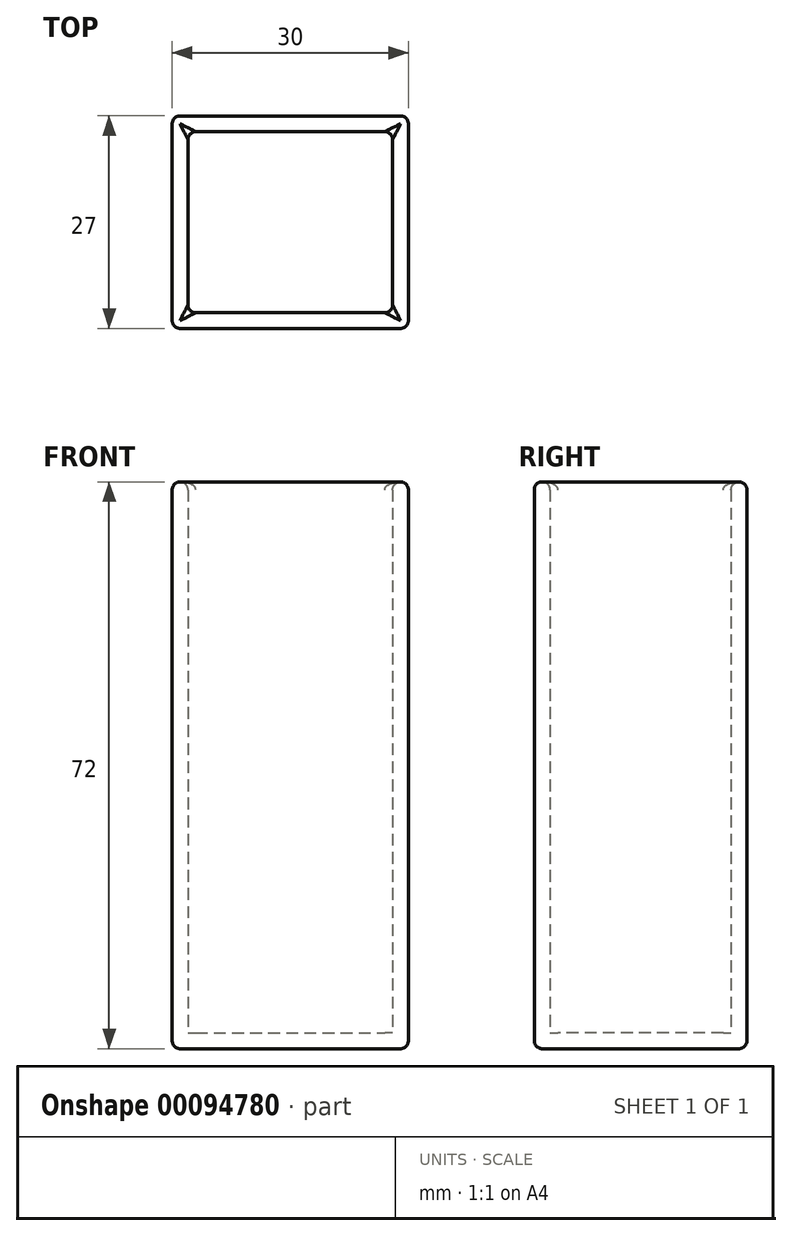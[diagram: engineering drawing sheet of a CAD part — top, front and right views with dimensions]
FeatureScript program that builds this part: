
annotation { "Feature Type Name" : "Feature", "Feature Type Description" : "" }
export const myFeature = defineFeature(function(context is Context, id is Id, definition is map)
    precondition{}
    {
        {
            var Q0;
            Q0=qCreatedBy(makeId("Top.planeOp"),FACE);
            var sketch = newSketch(context, id + "F0", { "sketchPlane" : qUnion([Q0])});
            skLineSegment(sketch, "E0.bottom", {"start": v(-23.26, 7.45) * mm, "end": v(2.74, 7.45) * mm});
            skLineSegment(sketch, "E0.top", {"start": v(-23.26, -15.55) * mm, "end": v(2.74, -15.55) * mm});
            skLineSegment(sketch, "E0.left", {"start": v(-23.26, 7.45) * mm, "end": v(-23.26, -15.55) * mm});
            skLineSegment(sketch, "E0.right", {"start": v(2.74, 7.45) * mm, "end": v(2.74, -15.55) * mm});
            skLineSegment(sketch, "E1.0", {"start": v(-25.26, 9.45) * mm, "end": v(4.74, 9.45) * mm});
            skLineSegment(sketch, "E1.1", {"start": v(-25.26, 9.45) * mm, "end": v(-25.26, -17.55) * mm});
            skLineSegment(sketch, "E1.2", {"start": v(-25.26, -17.55) * mm, "end": v(4.74, -17.55) * mm});
            skLineSegment(sketch, "E1.3", {"start": v(4.74, 9.45) * mm, "end": v(4.74, -17.55) * mm});
            skSolve(sketch);
        }
        {
            var Q0;
            Q0=makeQuery(id+"F0.imprint","IMPRINT",FACE,{"disambiguationData":[TD([[makeQuery(id+"F0.imprint","IMPRINT",EDGE,{"derivedFrom":sQuery(id+"F0.wireOp",EDGE,"E0.bottom")}),1.0]])]});
            extrude(context, id + "F1", {"entities" : qUnion([Q0]), "depth" : 70 * mm});
        }
        {
            var Q0;
            Q0=makeQuery(id+"F1.opExtrude","CAP_FACE",FACE,{"disambiguationData":[OSD([sQuery(id+"F0.wireOp",EDGE,"E0.bottom"),sQuery(id+"F0.wireOp",EDGE,"E0.top"),sQuery(id+"F0.wireOp",EDGE,"E0.left"),sQuery(id+"F0.wireOp",EDGE,"E0.right"),sQuery(id+"F0.wireOp",EDGE,"E1.0"),sQuery(id+"F0.wireOp",EDGE,"E1.1"),sQuery(id+"F0.wireOp",EDGE,"E1.2"),sQuery(id+"F0.wireOp",EDGE,"E1.3")])],"isStart":true});
            var sketch = newSketch(context, id + "F2", { "sketchPlane" : qUnion([Q0])});
            skLineSegment(sketch, "E2.bottom", {"start": v(-25.26, -9.45) * mm, "end": v(4.74, -9.45) * mm});
            skLineSegment(sketch, "E2.top", {"start": v(-25.26, 17.55) * mm, "end": v(4.74, 17.55) * mm});
            skLineSegment(sketch, "E2.left", {"start": v(-25.26, -9.45) * mm, "end": v(-25.26, 17.55) * mm});
            skLineSegment(sketch, "E2.right", {"start": v(4.74, -9.45) * mm, "end": v(4.74, 17.55) * mm});
            skSolve(sketch);
        }
        {
            var Q0;
            Q0 = qSketchRegion(id + "F2", true);
            extrude(context, id + "F3", {"entities" : qUnion([Q0]), "operationType" : NewBodyOperationType.ADD, "depth" : 2 * mm});
        }
        {
            var Q0;
            Q0=makeQuery(id+"F3.opExtrude","CAP_FACE",FACE,{"disambiguationData":[OSD([sQuery(id+"F2.wireOp",EDGE,"E2.bottom"),sQuery(id+"F2.wireOp",EDGE,"E2.top"),sQuery(id+"F2.wireOp",EDGE,"E2.left"),sQuery(id+"F2.wireOp",EDGE,"E2.right")])],"isStart":false});
            var Q1;
            Q1=makeQuery(id+"F3.boolean.opBoolean","MERGE",EDGE,{"derivedFrom":[makeQuery(id+"F1.opExtrude","SWEPT_EDGE",EDGE,{"disambiguationData":[OSD([sQuery(id+"F0.wireOp",EDGE,"E1.1"),sQuery(id+"F0.wireOp",EDGE,"E1.2")])]}),makeQuery(id+"F3.opExtrude","SWEPT_EDGE",EDGE,{"disambiguationData":[OSD([sQuery(id+"F2.wireOp",EDGE,"E2.top"),sQuery(id+"F2.wireOp",EDGE,"E2.left")])]})]});
            var Q2;
            Q2=makeQuery(id+"F3.boolean.opBoolean","MERGE",EDGE,{"derivedFrom":[makeQuery(id+"F1.opExtrude","SWEPT_EDGE",EDGE,{"disambiguationData":[OSD([sQuery(id+"F0.wireOp",EDGE,"E1.0"),sQuery(id+"F0.wireOp",EDGE,"E1.1")])]}),makeQuery(id+"F3.opExtrude","SWEPT_EDGE",EDGE,{"disambiguationData":[OSD([sQuery(id+"F2.wireOp",EDGE,"E2.bottom"),sQuery(id+"F2.wireOp",EDGE,"E2.left")])]})]});
            var Q3;
            Q3=makeQuery(id+"F3.boolean.opBoolean","MERGE",EDGE,{"derivedFrom":[makeQuery(id+"F1.opExtrude","SWEPT_EDGE",EDGE,{"disambiguationData":[OSD([sQuery(id+"F0.wireOp",EDGE,"E1.2"),sQuery(id+"F0.wireOp",EDGE,"E1.3")])]}),makeQuery(id+"F3.opExtrude","SWEPT_EDGE",EDGE,{"disambiguationData":[OSD([sQuery(id+"F2.wireOp",EDGE,"E2.top"),sQuery(id+"F2.wireOp",EDGE,"E2.right")])]})]});
            var Q4;
            Q4=makeQuery(id+"F3.boolean.opBoolean","MERGE",EDGE,{"derivedFrom":[makeQuery(id+"F1.opExtrude","SWEPT_EDGE",EDGE,{"disambiguationData":[OSD([sQuery(id+"F0.wireOp",EDGE,"E1.0"),sQuery(id+"F0.wireOp",EDGE,"E1.3")])]}),makeQuery(id+"F3.opExtrude","SWEPT_EDGE",EDGE,{"disambiguationData":[OSD([sQuery(id+"F2.wireOp",EDGE,"E2.bottom"),sQuery(id+"F2.wireOp",EDGE,"E2.right")])]})]});
            var Q5;
            Q5=makeQuery(id+"F1.opExtrude","CAP_EDGE",EDGE,{"disambiguationData":[OSD([sQuery(id+"F0.wireOp",EDGE,"E1.2")])],"isStart":false});
            var Q6;
            Q6=makeQuery(id+"F1.opExtrude","CAP_EDGE",EDGE,{"disambiguationData":[OSD([sQuery(id+"F0.wireOp",EDGE,"E1.3")])],"isStart":false});
            var Q7;
            Q7=makeQuery(id+"F1.opExtrude","CAP_EDGE",EDGE,{"disambiguationData":[OSD([sQuery(id+"F0.wireOp",EDGE,"E1.0")])],"isStart":false});
            var Q8;
            Q8=makeQuery(id+"F1.opExtrude","CAP_EDGE",EDGE,{"disambiguationData":[OSD([sQuery(id+"F0.wireOp",EDGE,"E1.1")])],"isStart":false});
            var Q9;
            Q9=makeQuery(id+"F1.opExtrude","CAP_EDGE",EDGE,{"disambiguationData":[OSD([sQuery(id+"F0.wireOp",EDGE,"E0.top")])],"isStart":false});
            var Q10;
            Q10=makeQuery(id+"F1.opExtrude","CAP_EDGE",EDGE,{"disambiguationData":[OSD([sQuery(id+"F0.wireOp",EDGE,"E0.right")])],"isStart":false});
            var Q11;
            Q11=makeQuery(id+"F1.opExtrude","CAP_EDGE",EDGE,{"disambiguationData":[OSD([sQuery(id+"F0.wireOp",EDGE,"E0.bottom")])],"isStart":false});
            var Q12;
            Q12=makeQuery(id+"F1.opExtrude","CAP_EDGE",EDGE,{"disambiguationData":[OSD([sQuery(id+"F0.wireOp",EDGE,"E0.left")])],"isStart":false});
            fillet(context, id + "F4", {"entities" : qUnion([Q0, Q1, Q2, Q3, Q4, Q5, Q6, Q7, Q8, Q9, Q10, Q11, Q12]), "radius" : 1 * mm, "tangentPropagation" : true, "allowEdgeOverflow" : false});
        }
        {
            var Q0;
            Q0=makeQuery(id+"F1.opExtrude","SWEPT_EDGE",EDGE,{"disambiguationData":[OSD([sQuery(id+"F0.wireOp",EDGE,"E0.top"),sQuery(id+"F0.wireOp",EDGE,"E0.left")])]});
            var Q1;
            Q1=makeQuery(id+"F1.opExtrude","CAP_EDGE",EDGE,{"disambiguationData":[OSD([sQuery(id+"F0.wireOp",EDGE,"E0.top")])],"isStart":true});
            var Q2;
            Q2=makeQuery(id+"F1.opExtrude","SWEPT_EDGE",EDGE,{"disambiguationData":[OSD([sQuery(id+"F0.wireOp",EDGE,"E0.top"),sQuery(id+"F0.wireOp",EDGE,"E0.right")])]});
            var Q3;
            Q3=makeQuery(id+"F1.opExtrude","SWEPT_EDGE",EDGE,{"disambiguationData":[OSD([sQuery(id+"F0.wireOp",EDGE,"E0.bottom"),sQuery(id+"F0.wireOp",EDGE,"E0.right")])]});
            var Q4;
            Q4=makeQuery(id+"F1.opExtrude","SWEPT_EDGE",EDGE,{"disambiguationData":[OSD([sQuery(id+"F0.wireOp",EDGE,"E0.bottom"),sQuery(id+"F0.wireOp",EDGE,"E0.left")])]});
            var Q5;
            Q5=makeQuery(id+"F1.opExtrude","CAP_EDGE",EDGE,{"disambiguationData":[OSD([sQuery(id+"F0.wireOp",EDGE,"E0.left")])],"isStart":true});
            var Q6;
            Q6=makeQuery(id+"F1.opExtrude","CAP_EDGE",EDGE,{"disambiguationData":[OSD([sQuery(id+"F0.wireOp",EDGE,"E0.bottom")])],"isStart":true});
            fillet(context, id + "F5", {"entities" : qUnion([Q0, Q1, Q2, Q3, Q4, Q5, Q6]), "radius" : 1 * mm, "tangentPropagation" : true, "allowEdgeOverflow" : false});
        }
    });
